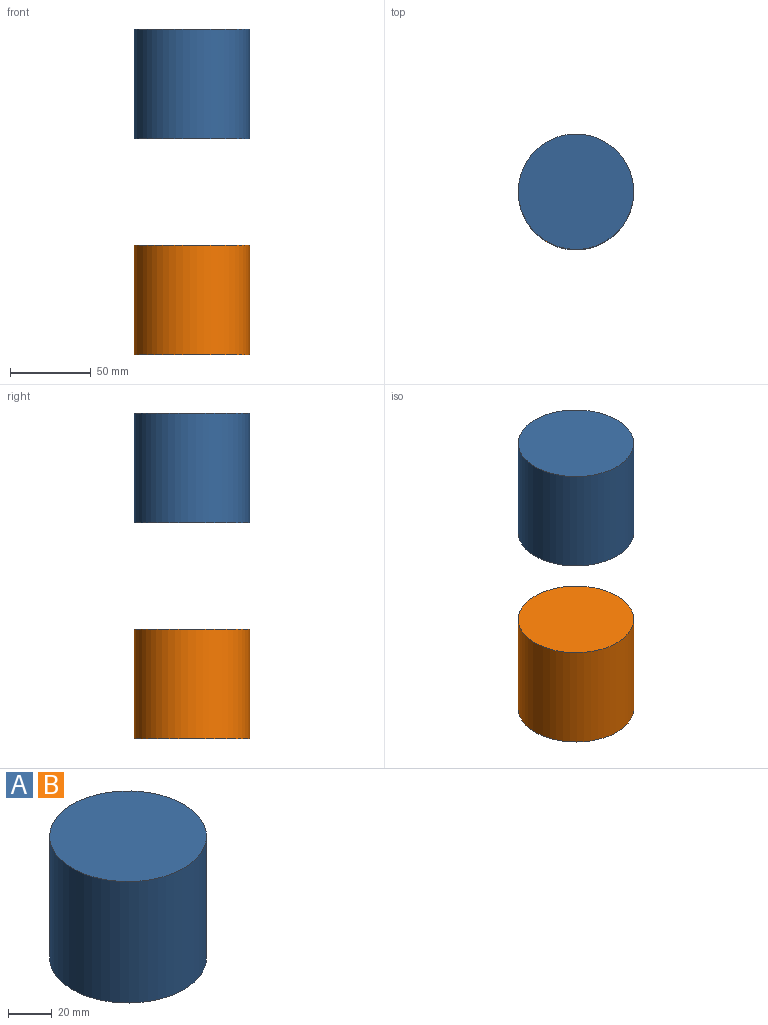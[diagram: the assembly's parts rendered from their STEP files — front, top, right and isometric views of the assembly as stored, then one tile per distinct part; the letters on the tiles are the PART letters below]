
ASSEMBLY  parts=2 mates=1
PART A: 3 faces, bbox 71.4x71.4x67.6 mm
  f0: cylinder r=35.68mm len=71.36mm, axis (0,0,-1), area 15154.5mm2, adj f1,f2
  f1: plane 71.36x71.36mm, normal (0,0,1), area 3999.3mm2, adj f0
  f2: plane 71.36x71.36mm, normal (0,0,-1), area 3999.3mm2, adj f0
PART B: same geometry as A
PLACE A rot(axis=(1,0,0),180deg) t=(32.94,86.54,171.22)mm
PLACE B t=(32.94,86.54,-29.72)mm fixed
MATE slider A.f0 <-> B.f0  axis (0,0,-1) through (32.94,86.54,103.62)mm
